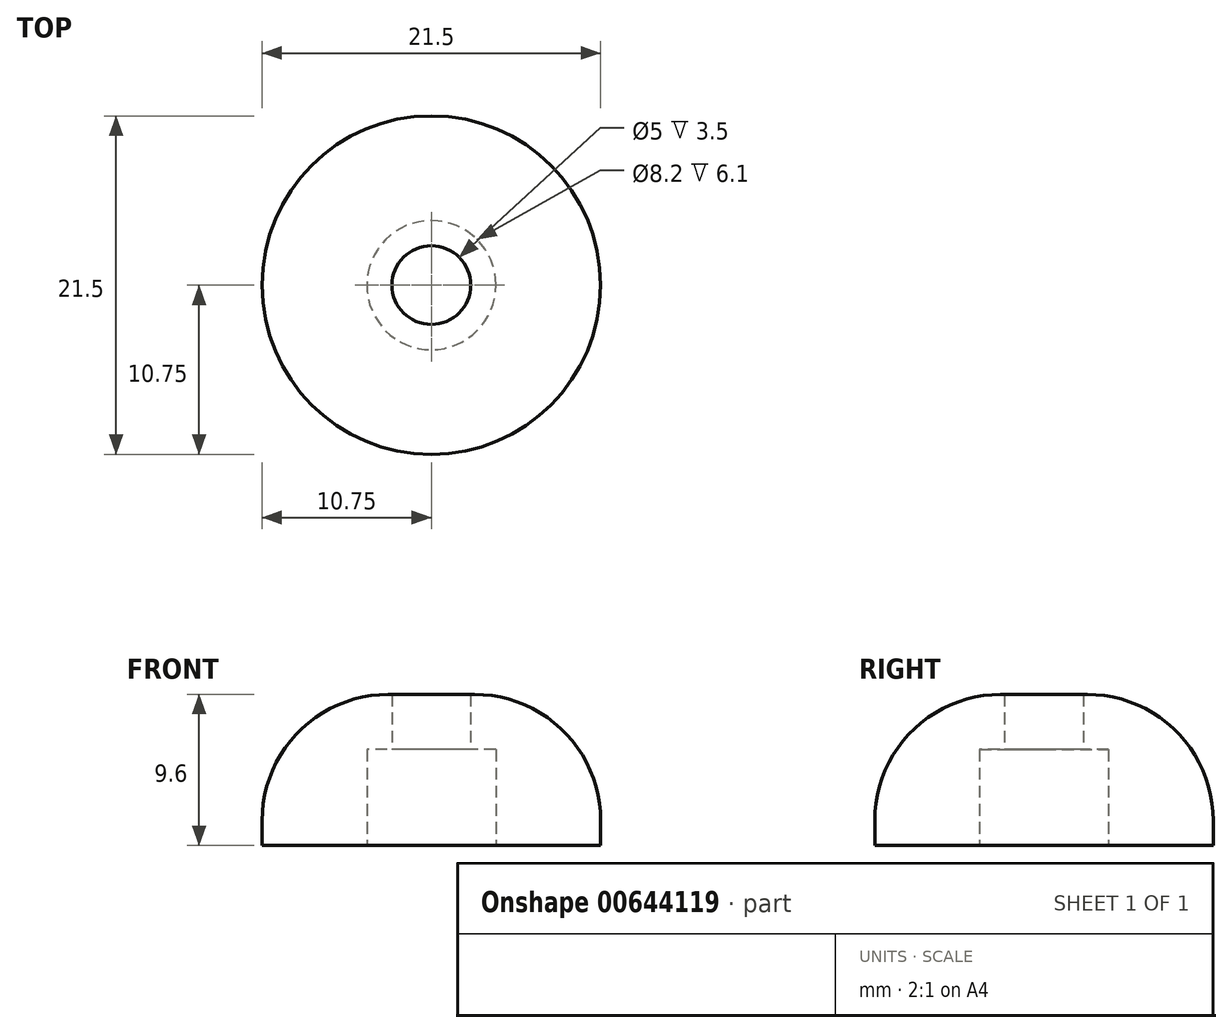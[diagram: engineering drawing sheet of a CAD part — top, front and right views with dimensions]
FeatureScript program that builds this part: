
annotation { "Feature Type Name" : "Feature", "Feature Type Description" : "" }
export const myFeature = defineFeature(function(context is Context, id is Id, definition is map)
    precondition{}
    {
        {
            var Q0;
            Q0=qCreatedBy(makeId("Top.planeOp"),FACE);
            var sketch = newSketch(context, id + "F0", { "sketchPlane" : qUnion([Q0])});
            skCircle(sketch, "E0", {"center": v(0, 0) * mm, "radius": 10.75 * mm});
            skCircle(sketch, "E1", {"center": v(0, 0) * mm, "radius": 2.5 * mm});
            skCircle(sketch, "E2", {"center": v(0, 0) * mm, "radius": 4.1 * mm});
            skSolve(sketch);
        }
        {
            var Q0;
            Q0=makeQuery(id+"F0.imprint","IMPRINT",FACE,{"disambiguationData":[TD([[makeQuery(id+"F0.imprint","IMPRINT",EDGE,{"derivedFrom":sQuery(id+"F0.wireOp",EDGE,"E0")}),1.0]])]});
            var Q1;
            Q1=makeQuery(id+"F0.imprint","IMPRINT",FACE,{"disambiguationData":[TD([[makeQuery(id+"F0.imprint","IMPRINT",EDGE,{"derivedFrom":sQuery(id+"F0.wireOp",EDGE,"E1")}),-1.0]])]});
            extrude(context, id + "F1", {"entities" : qUnion([Q0, Q1]), "depth" : 9.6 * mm, "offsetDistance" : 25 * mm});
        }
        {
            var Q0;
            Q0=makeQuery(id+"F1.opExtrude","CAP_EDGE",EDGE,{"disambiguationData":[OSD([sQuery(id+"F0.wireOp",EDGE,"E0")])],"isStart":false});
            fillet(context, id + "F2", {"entities" : qUnion([Q0]), "radius" : 8 * mm, "tangentPropagation" : true, "allowEdgeOverflow" : false});
        }
        {
            var Q0;
            Q0=makeQuery(id+"F0.imprint","IMPRINT",FACE,{"disambiguationData":[TD([[makeQuery(id+"F0.imprint","IMPRINT",EDGE,{"derivedFrom":sQuery(id+"F0.wireOp",EDGE,"E1")}),1.0]])]});
            extrude(context, id + "F3", {"entities" : qUnion([Q0]), "operationType" : NewBodyOperationType.REMOVE, "oppositeDirection" : true, "depth" : 25 * mm, "offsetDistance" : 25 * mm});
        }
        {
            var Q0;
            Q0=makeQuery(id+"F0.imprint","IMPRINT",FACE,{"disambiguationData":[TD([[makeQuery(id+"F0.imprint","IMPRINT",EDGE,{"derivedFrom":sQuery(id+"F0.wireOp",EDGE,"E1")}),-1.0]])]});
            extrude(context, id + "F4", {"entities" : qUnion([Q0]), "operationType" : NewBodyOperationType.REMOVE, "depth" : 6.1 * mm, "offsetDistance" : 25 * mm, "hasSecondDirection" : true, "secondDirectionOppositeDirection" : true, "secondDirectionDepth" : 13.5 * mm});
        }
    });
